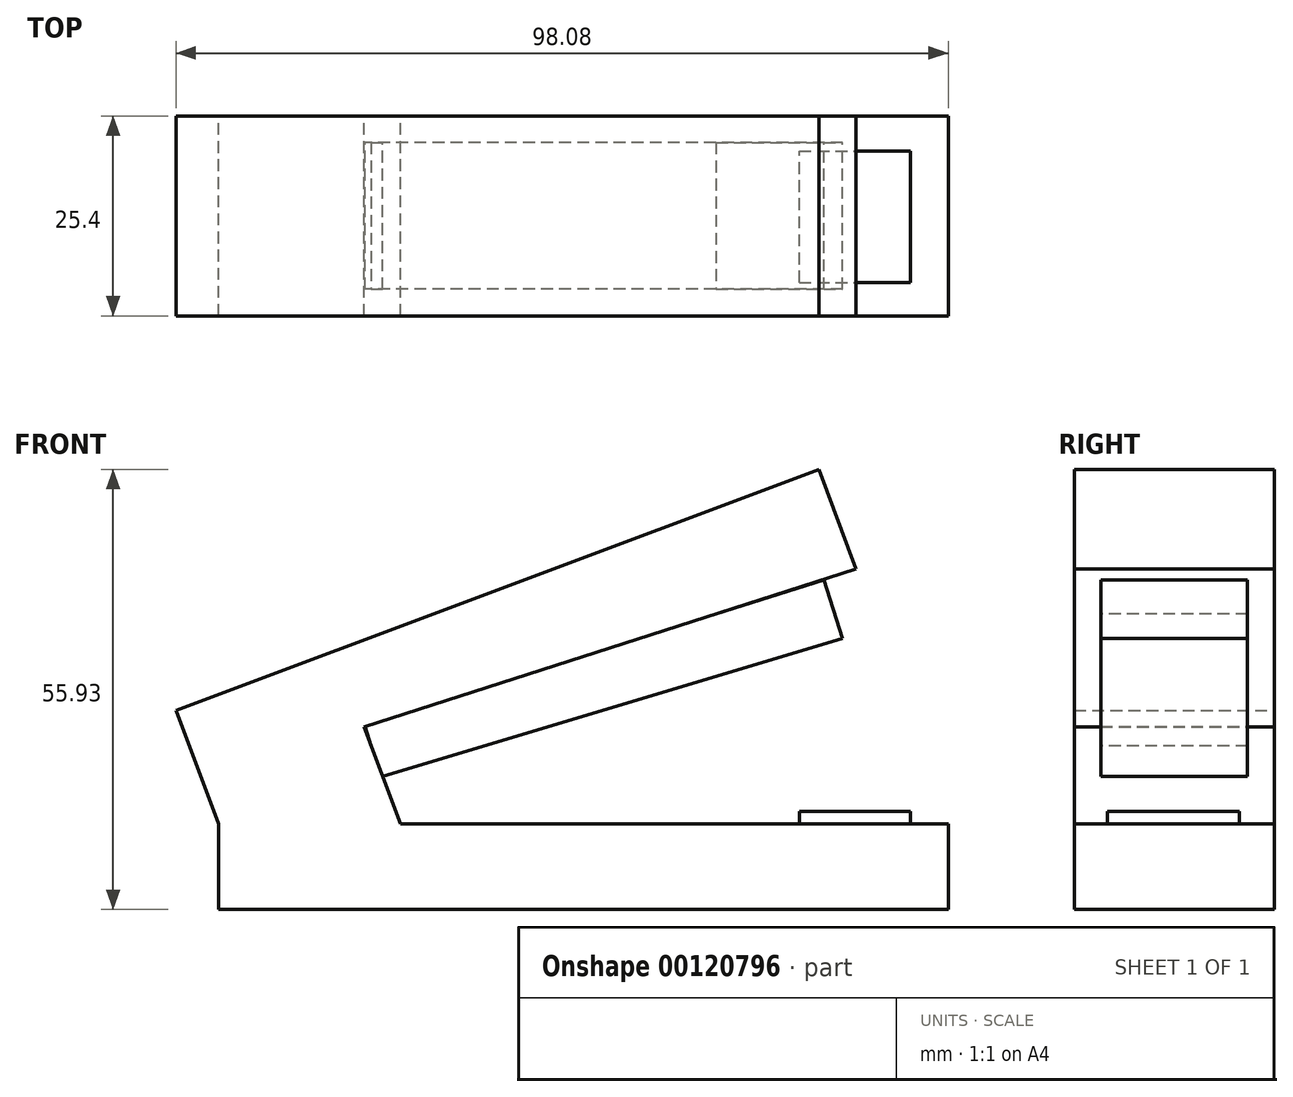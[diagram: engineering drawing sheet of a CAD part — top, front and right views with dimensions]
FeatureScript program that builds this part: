
annotation { "Feature Type Name" : "Feature", "Feature Type Description" : "" }
export const myFeature = defineFeature(function(context is Context, id is Id, definition is map)
    precondition{}
    {
        {
            var Q0;
            Q0=qCreatedBy(makeId("Front.planeOp"),FACE);
            var sketch = newSketch(context, id + "F0", { "sketchPlane" : qUnion([Q0])});
            skLineSegment(sketch, "E0.bottom", {"start": v(-48.57, 10.88) * mm, "end": v(44.1, 10.88) * mm});
            skLineSegment(sketch, "E0.top", {"start": v(-48.57, 0) * mm, "end": v(44.1, 0) * mm});
            skLineSegment(sketch, "E0.left", {"start": v(-48.57, 10.88) * mm, "end": v(-48.57, 0) * mm});
            skLineSegment(sketch, "E0.right", {"start": v(44.1, 10.88) * mm, "end": v(44.1, 0) * mm});
            skLineSegment(sketch, "E1", {"start": v(-48.57, 10.88) * mm, "end": v(-50.36, 15.64) * mm});
            skLineSegment(sketch, "E2", {"start": v(-50.36, 15.64) * mm, "end": v(-30.11, 23.24) * mm});
            skLineSegment(sketch, "E3", {"start": v(-30.11, 23.24) * mm, "end": v(-25.48, 10.88) * mm});
            skLineSegment(sketch, "E4", {"start": v(-50.36, 15.64) * mm, "end": v(-53.98, 25.31) * mm});
            skLineSegment(sketch, "E5", {"start": v(-53.98, 25.31) * mm, "end": v(27.66, 55.93) * mm});
            skLineSegment(sketch, "E6", {"start": v(27.66, 55.93) * mm, "end": v(32.4, 43.29) * mm});
            skLineSegment(sketch, "E7", {"start": v(32.4, 43.29) * mm, "end": v(-30.11, 23.24) * mm});
            skSolve(sketch);
        }
        {
            var Q0;
            Q0=qCreatedBy(makeId("Front.planeOp"),FACE);
            var sketch = newSketch(context, id + "F1", { "sketchPlane" : qUnion([Q0])});
            skLineSegment(sketch, "E8", {"start": v(28.3, 41.87) * mm, "end": v(30.7, 34.42) * mm});
            skLineSegment(sketch, "E9", {"start": v(30.7, 34.42) * mm, "end": v(-28.01, 16.84) * mm});
            skLineSegment(sketch, "E10", {"start": v(-28.01, 16.84) * mm, "end": v(-30.04, 23.62) * mm});
            skLineSegment(sketch, "E11", {"start": v(-30.04, 23.62) * mm, "end": v(28.3, 41.87) * mm});
            skSolve(sketch);
        }
        {
            var Q0;
            Q0 = qSketchRegion(id + "F0", true);
            extrude(context, id + "F2", {"entities" : qUnion([Q0]), "endBound" : BoundingType.SYMMETRIC, "depth" : 25.4 * mm});
        }
        {
            var Q0;
            Q0 = qSketchRegion(id + "F1", true);
            extrude(context, id + "F3", {"entities" : qUnion([Q0]), "operationType" : NewBodyOperationType.ADD, "endBound" : BoundingType.SYMMETRIC, "depth" : 18.65 * mm});
        }
        {
            var Q0;
            Q0=makeQuery(id+"F2.opExtrude","SWEPT_FACE",FACE,{"disambiguationData":[OSD([sQuery(id+"F0.wireOp",EDGE,"E0.bottom")])]});
            var sketch = newSketch(context, id + "F4", { "sketchPlane" : qUnion([Q0])});
            skLineSegment(sketch, "E12.bottom", {"start": v(25.19, -8.47) * mm, "end": v(39.3, -8.47) * mm});
            skLineSegment(sketch, "E12.top", {"start": v(25.19, 8.26) * mm, "end": v(39.3, 8.26) * mm});
            skLineSegment(sketch, "E12.left", {"start": v(25.19, -8.47) * mm, "end": v(25.19, 8.26) * mm});
            skLineSegment(sketch, "E12.right", {"start": v(39.3, -8.47) * mm, "end": v(39.3, 8.26) * mm});
            skSolve(sketch);
        }
        {
            var Q0;
            Q0 = qSketchRegion(id + "F4", true);
            extrude(context, id + "F5", {"entities" : qUnion([Q0]), "operationType" : NewBodyOperationType.ADD, "depth" : 1.63 * mm});
        }
    });
